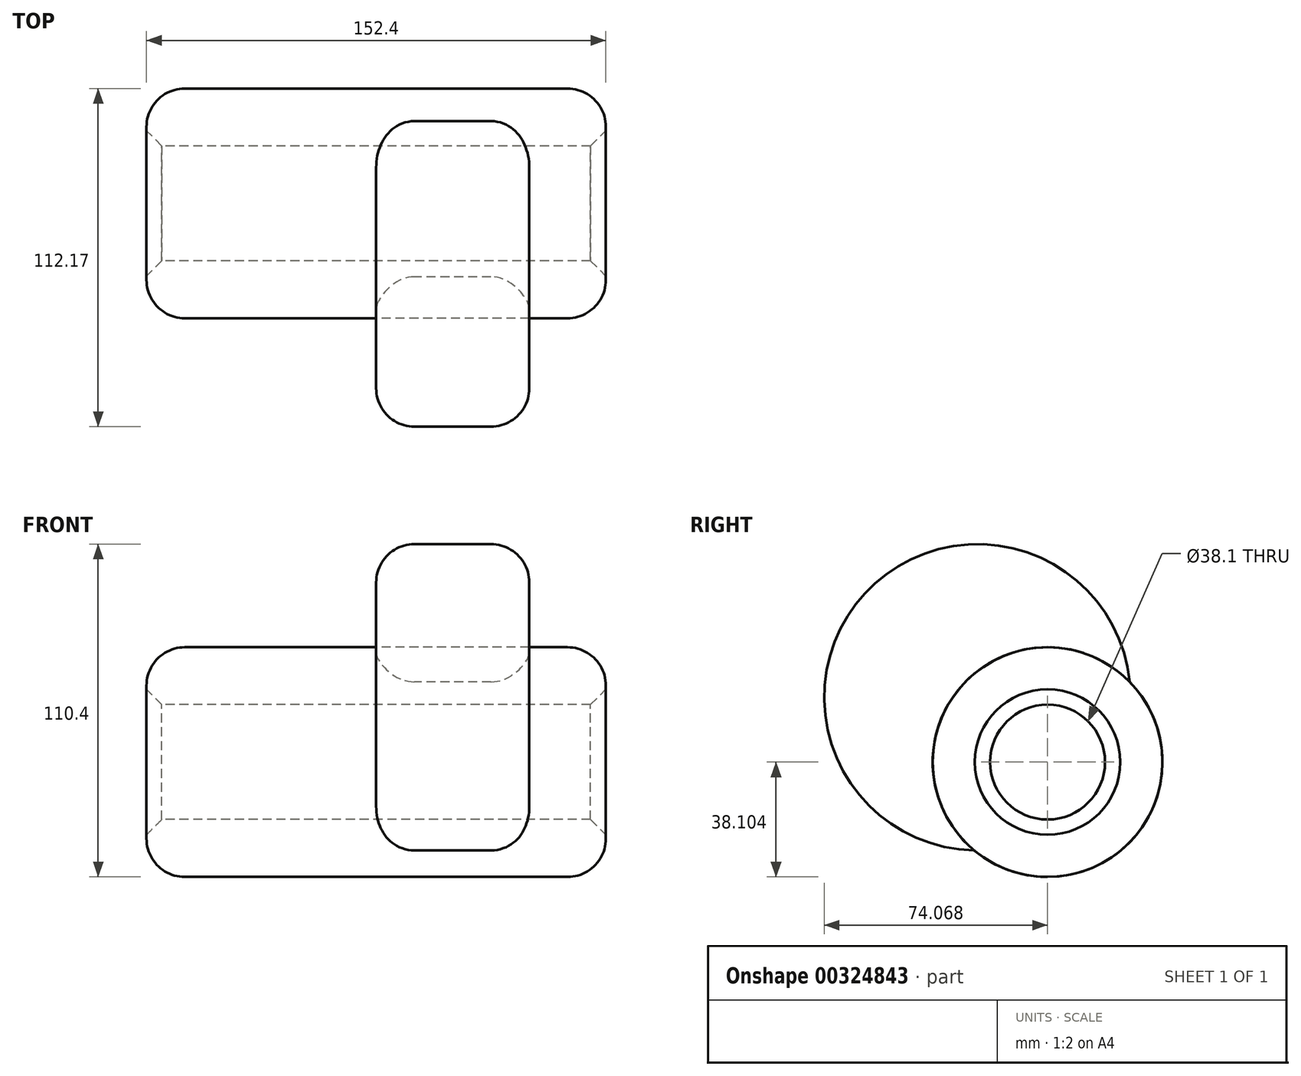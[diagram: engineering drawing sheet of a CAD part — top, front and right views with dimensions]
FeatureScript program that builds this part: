
annotation { "Feature Type Name" : "Feature", "Feature Type Description" : "" }
export const myFeature = defineFeature(function(context is Context, id is Id, definition is map)
    precondition{}
    {
        {
            var Q0;
            Q0=qCreatedBy(makeId("Right.planeOp"),FACE);
            var sketch = newSketch(context, id + "F0", { "sketchPlane" : qUnion([Q0])});
            skCircle(sketch, "E0", {"center": v(0, -2.95) * mm, "radius": 50.8 * mm});
            skCircle(sketch, "E1", {"center": v(23.27, -24.45) * mm, "radius": 38.1 * mm});
            skSolve(sketch);
        }
        {
            var Q0;
            {var subQ0=sQuery(id+"F0.wireOp",EDGE,"E1");var subQ1=sQuery(id+"F0.wireOp",EDGE,"E0");var subQ2=makeQuery(id+"F0.imprint","INTERSECT",VERTEX,{"disambiguationData":[OD(0.0)],"derivedFrom":[subQ1,subQ0]});Q0=makeQuery(id+"F0.imprint","IMPRINT",FACE,{"disambiguationData":[TD([[makeQuery(id+"F0.imprint","IMPRINT",EDGE,{"disambiguationData":[TD([[subQ2,1.0]])],"derivedFrom":subQ1}),1.0]])]});}
            extrude(context, id + "F1", {"entities" : qUnion([Q0]), "depth" : 50.8 * mm});
        }
        {
            var Q0;
            {var subQ0=sQuery(id+"F0.wireOp",EDGE,"E1");var subQ1=sQuery(id+"F0.wireOp",EDGE,"E0");var subQ2=makeQuery(id+"F0.imprint","INTERSECT",VERTEX,{"disambiguationData":[OD(0.0)],"derivedFrom":[subQ1,subQ0]});Q0=makeQuery(id+"F0.imprint","IMPRINT",FACE,{"disambiguationData":[TD([[makeQuery(id+"F0.imprint","IMPRINT",EDGE,{"disambiguationData":[TD([[subQ2,-1.0]])],"derivedFrom":subQ1}),-1.0]])]});}
            var Q1;
            {var subQ0=sQuery(id+"F0.wireOp",EDGE,"E1");var subQ1=sQuery(id+"F0.wireOp",EDGE,"E0");var subQ2=makeQuery(id+"F0.imprint","INTERSECT",VERTEX,{"disambiguationData":[OD(0.0)],"derivedFrom":[subQ1,subQ0]});Q1=makeQuery(id+"F0.imprint","IMPRINT",FACE,{"disambiguationData":[TD([[makeQuery(id+"F0.imprint","IMPRINT",EDGE,{"disambiguationData":[TD([[subQ2,-1.0]])],"derivedFrom":subQ1}),1.0]])]});}
            extrude(context, id + "F2", {"entities" : qUnion([Q0, Q1]), "endBound" : BoundingType.SYMMETRIC, "depth" : 152.4 * mm});
        }
        {
            var Q0;
            Q0=makeQuery(id+"F2.opExtrude","SWEPT_FACE",FACE,{"disambiguationData":[OSD([sQuery(id+"F0.wireOp",EDGE,"E1")])]});
            var Q1;
            Q1=makeQuery(id+"F1.opExtrude","CAP_EDGE",EDGE,{"disambiguationData":[OSD([sQuery(id+"F0.wireOp",EDGE,"E0")])],"isStart":true});
            var Q2;
            Q2=makeQuery(id+"F1.opExtrude","CAP_EDGE",EDGE,{"disambiguationData":[OSD([sQuery(id+"F0.wireOp",EDGE,"E0")])],"isStart":false});
            fillet(context, id + "F3", {"entities" : qUnion([Q0, Q1, Q2]), "radius" : 12.7 * mm, "tangentPropagation" : true, "allowEdgeOverflow" : false});
        }
        {
            var Q0;
            Q0=makeQuery(id+"F2.opExtrude","CAP_FACE",FACE,{"disambiguationData":[OSD([sQuery(id+"F0.wireOp",EDGE,"E1")])],"isStart":true});
            var sketch = newSketch(context, id + "F4", { "sketchPlane" : qUnion([Q0])});
            skCircle(sketch, "E2", {"center": v(-23.27, -24.45) * mm, "radius": 19.05 * mm});
            skSolve(sketch);
        }
        {
            var Q0;
            Q0 = qSketchRegion(id + "F4", true);
            extrude(context, id + "F5", {"entities" : qUnion([Q0]), "operationType" : NewBodyOperationType.REMOVE, "endBound" : BoundingType.THROUGH_ALL, "oppositeDirection" : true, "depth" : 25.4 * mm});
        }
        {
            var Q0;
            Q0=makeQuery(id+"F5.boolean.opBoolean","COPY",FACE,{"derivedFrom":makeQuery(id+"F5.opExtrude","SWEPT_FACE",FACE,{"disambiguationData":[OSD([sQuery(id+"F4.wireOp",EDGE,"E2")])]})});
            chamfer(context, id + "F6", {"entities" : qUnion([Q0]), "width" : 5.08 * mm, "tangentPropagation" : true});
        }
    });
